# Revit family: IS_Finesse_E3401_BIM_NL
name_source: partatom
category: Plumbing Fixtures
units: mm (PartAtom-declared; Revit-internal decimal feet)

## family parameters
Cut with Voids When Loaded = No
Host = Face
Maintain Annotation Orientation = No
OmniClass Number = 23.45.05.14.21.11
OmniClass Title = Bath/Shower Units
Part Type = Normal
Room Calculation Point = No
Round Connector Dimension = Use Diameter
Shared = Yes

## types (6) — shared parameters
Accessories = https://www.idealstandard.nl
Afmetingen = 400 x 505 x 540mm
AfstandsEenheid = millimeter
AreaUnits = millimeters
Artikelomschrijving = FINESSE | Kast 400x505x540 mm
Assembly Code = C1030200
AssetType = Fixed
Auteur = Ideal Standard
BIMObjectName = ISI_IdealStandard_Furniture_Finesse_E3401
BREEAM = No
Beschrijvinggarantie = Fabrieksgarantie
BimObjectNaam = ISI_IdealStandard_Furniture_Finesse_E3401
Brand = Ideal Standard
Breedte = 400
ConnectionType = Plumbing
CurrencyUnit = €
Default Elevation = 1219 mm
Description = FINESSE | Cabinet 400x505x540 mm
Diepte = 504,999999999982
DurationUnit = year
DuurEenheid = jaar
ECA = No
EPD = https://www.idealstandard.nl
ExpectedLife = 30
Garantieunits = Jaar
GemaaktOp = 2024/09/04
Help = https://www.idealstandard.nl
Hoogte = 540,000000000002
Hulp = https://www.idealstandard.nl
IfcExportAs = IfcFurnitureType
Installatieinstructies = https://www.idealstandard.nl
InstallationInstructions = https://www.idealstandard.nl
Lengte = 504,999999999982
LinearUnits = millimeters
Manufacturer = Ideal Standard
ManufacturerURL = https://www.idealstandard.nl
Materiaal = hout
Merk = Ideal Standard
ModelReference = FINESSE | Cabinet 400x505x540 mm
NBSDescription = Baths
Name = ISI_Furniture_Finesse_E3401_IdealStandard
NominalDepth = 505 mm
NominalHeight = 540 mm  [stored 1.77165 ft]
NominalLength = 505 mm
NominalWidth = 400 mm  [stored 1.31234 ft]
ProductInformation = https://www.idealstandard.nl
ProductSoort = Meubilair
Productinformatie = https://www.idealstandard.nl
Shape = Rectangular
Size = 400 x 505 x 540mm
Space = Internal
SpareParts = https://www.idealstandard.nl
TMV3 = No
Telefoonnummer = 077 355 08 08
Typeconnectie = Sanitair
URL = https://www.idealstandard.nl
Uniclass2015Code = Pr_40_20_76
Uniclass2015Title = Sanitary accessories
Uniclass2015Version = Products v1.34
Urlproducent = https://www.idealstandard.nl
ValutaEenheid = €
Versie = 1
Version = 1
VolumeUnits = Litres
Volumeunits = Liter
Vorm = Rechthoekig
WRAS = No
WarrantyDescription = Manufacturers Warranty
WarrantyDurationParts = 25
WarrantyDurationUnit = year
WarrantyGuarantorParts = https://www.idealstandard.nl
WaterEfficientProduct = No
Wisselstukken = https://www.idealstandard.nl
zero-valued in all types: Vervangingskosten

## per-type parameters (varying)
| type | Afwerking | Artikelnummer | Artikelreferentie | BarCode | Color | Eigenschappen | Features | Finish | Kleur | MAT | Model | ModelNumber | NettWeight | Nettogewicht |
| E3401UP - FINESSE OS UNIT 2DRWS 40X50CM GEMT | Greige mat | E3401UP | FINESSE / Kast 400x505x540 mm in mat greige afwerking / Voorgemonteerd, Duurzaam geproduceerd hout | 5017830565956 | greige matt | FINESSE / Kast 400x505x540 mm in mat greige afwerking / Voorgemonteerd, Duurzaam geproduceerd hout | FINESSE / Cabinet 400x505x540 mm in greige matt finish / Assembled, Sustainably sourced wood | greige matt | Greige mat | UP | E3401UP | E3401UP | 14.85 Kg | 14.85 Kg |
| E3401UQ - FINESSE OS UNIT 2DRWS 40X50CM ABMT | Mat asblauw | E3401UQ | FINESSE / Kast 400x505x540 mm in matt ashblue afwerking / Voorgemonteerd, Duurzaam geproduceerd hout | 5017830565963 | matt ashblue | FINESSE / Kast 400x505x540 mm in matt ashblue afwerking / Voorgemonteerd, Duurzaam geproduceerd hout | FINESSE / Cabinet 400x505x540 mm in matt ashblue finish / Assembled, Sustainably sourced wood | matt ashblue | Mat asblauw | UQ | E3401UQ | E3401UQ | 14.85 Kg | 14.85 Kg |
| E3401UR - FINESSE OS UNIT 2DRWS 40X50CM DKEM | Donkere iep | E3401UR | FINESSE / Kast 400x505x540 mm in dark elm afwerking / Voorgemonteerd, Duurzaam geproduceerd hout | 5017830565970 | dark elm | FINESSE / Kast 400x505x540 mm in dark elm afwerking / Voorgemonteerd, Duurzaam geproduceerd hout | FINESSE / Cabinet 400x505x540 mm in dark elm finish / Assembled, Sustainably sourced wood | dark elm | Donkere iep | UR | E3401UR | E3401UR | 14.71 Kg | 14.71 Kg |
| E3401US - FINESSE OS UNIT 2DRWS 40X50CM WOAK | Witte eik | E3401US | FINESSE / Kast 400x505x540 mm in white oak afwerking / Voorgemonteerd, Duurzaam geproduceerd hout | 5017830565987 | white oak | FINESSE / Kast 400x505x540 mm in white oak afwerking / Voorgemonteerd, Duurzaam geproduceerd hout | FINESSE / Cabinet 400x505x540 mm in white oak finish / Assembled, Sustainably sourced wood | white oak | Witte eik | US | E3401US | E3401US | 14.71 Kg | 14.71 Kg |
| E3401Y1 - FINESSE OS UNIT 2DRWS 40X50CM WHMT | Mat wit | E3401Y1 | FINESSE / Kast 400x505x540 mm in matt white afwerking / Voorgemonteerd, Duurzaam geproduceerd hout | 5017830565994 | matt white | FINESSE / Kast 400x505x540 mm in matt white afwerking / Voorgemonteerd, Duurzaam geproduceerd hout | FINESSE / Cabinet 400x505x540 mm in matt white finish / Assembled, Sustainably sourced wood | matt white | Mat wit | Y1 | E3401Y1 | E3401Y1 | 14.85 Kg | 14.85 Kg |
| E3401Y2 - FINESSE OS UNIT 2DRWS 40X50CM ANMT | Mat antraciet | E3401Y2 | FINESSE / Kast 400x505x540 mm in matt anthracite afwerking / Voorgemonteerd, Duurzaam geproduceerd hout | 5017830566007 | matt anthracite | FINESSE / Kast 400x505x540 mm in matt anthracite afwerking / Voorgemonteerd, Duurzaam geproduceerd hout | FINESSE / Cabinet 400x505x540 mm in matt anthracite finish / Assembled, Sustainably sourced wood | matt anthracite | Mat antraciet | Y2 | E3401Y2 | E3401Y2 | 14.85 Kg | 14.85 Kg |

note: [stored X ft] marks values corroborated as IEEE doubles in the binary element streams (Revit-internal decimal feet)

## geometry (parser evidence)
native form markers: Sweep x3
no freeform markers — native parametric forms only
